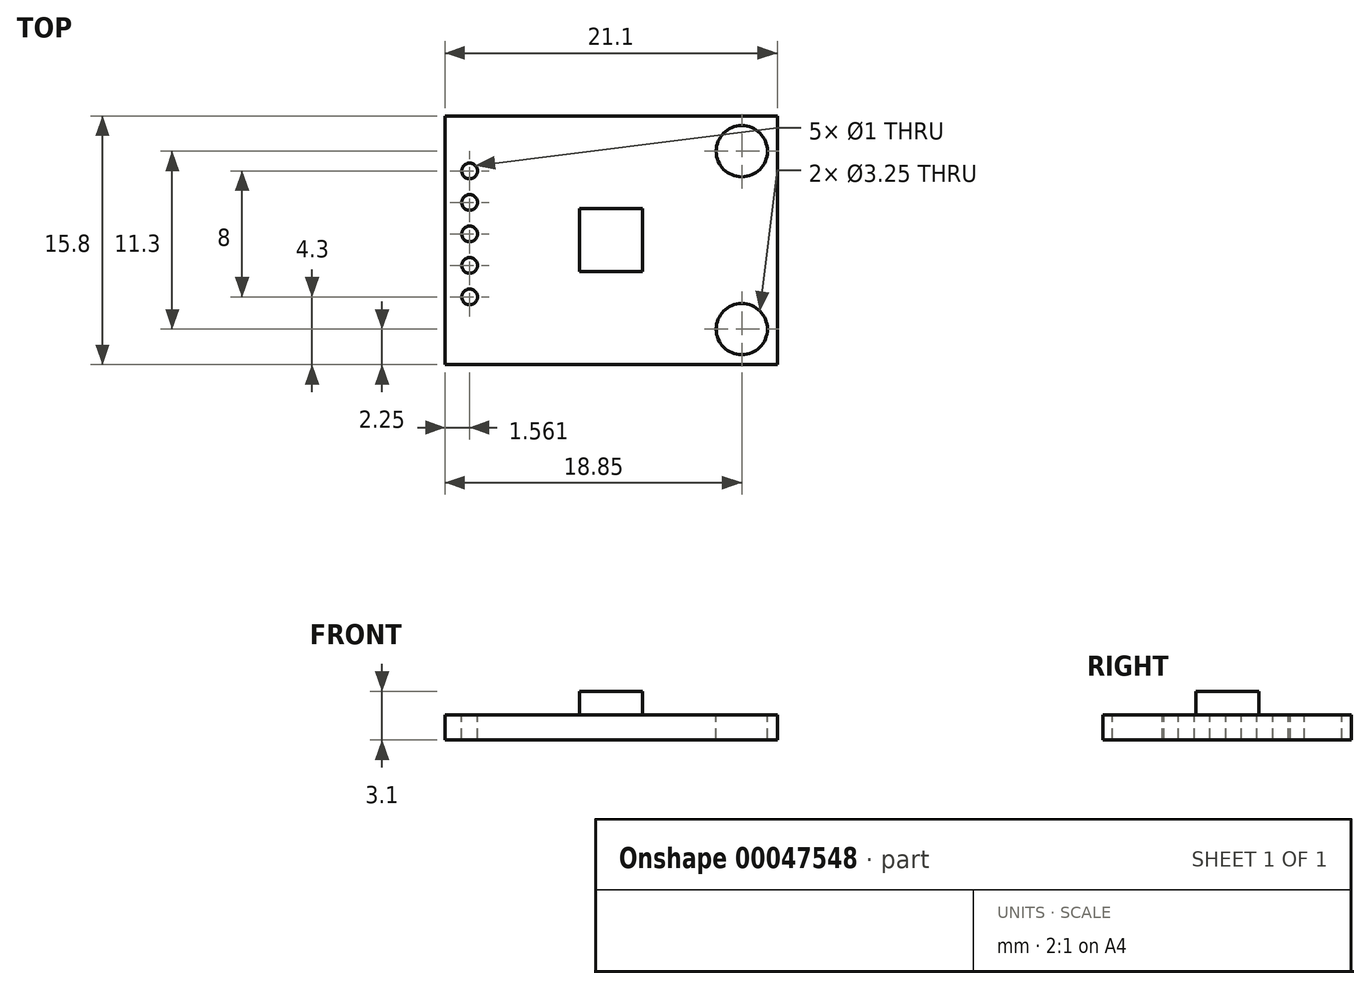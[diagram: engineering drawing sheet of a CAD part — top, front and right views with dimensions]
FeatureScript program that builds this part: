
annotation { "Feature Type Name" : "Feature", "Feature Type Description" : "" }
export const myFeature = defineFeature(function(context is Context, id is Id, definition is map)
    precondition{}
    {
        {
            var Q0;
            Q0=qCreatedBy(makeId("Top.planeOp"),FACE);
            var sketch = newSketch(context, id + "F0", { "sketchPlane" : qUnion([Q0])});
            skLineSegment(sketch, "E0.bottom", {"start": v(-10.55, 7.9) * mm, "end": v(10.55, 7.9) * mm});
            skLineSegment(sketch, "E0.top", {"start": v(-10.55, -7.9) * mm, "end": v(10.55, -7.9) * mm});
            skLineSegment(sketch, "E0.left", {"start": v(-10.55, 7.9) * mm, "end": v(-10.55, -7.9) * mm});
            skLineSegment(sketch, "E0.right", {"start": v(10.55, 7.9) * mm, "end": v(10.55, -7.9) * mm});
            skSolve(sketch);
        }
        {
            var Q0;
            Q0 = qSketchRegion(id + "F0", true);
            extrude(context, id + "F1", {"entities" : qUnion([Q0]), "depth" : 1.6 * mm});
        }
        {
            var Q0;
            Q0=makeQuery(id+"F1.opExtrude","CAP_FACE",FACE,{"disambiguationData":[OSD([sQuery(id+"F0.wireOp",EDGE,"E0.bottom"),sQuery(id+"F0.wireOp",EDGE,"E0.top"),sQuery(id+"F0.wireOp",EDGE,"E0.left"),sQuery(id+"F0.wireOp",EDGE,"E0.right")])],"isStart":false});
            var sketch = newSketch(context, id + "F2", { "sketchPlane" : qUnion([Q0])});
            skCircle(sketch, "E1", {"center": v(8.3, 5.65) * mm, "radius": 1.63 * mm});
            skCircle(sketch, "E2", {"center": v(8.3, -5.65) * mm, "radius": 1.63 * mm});
            skSolve(sketch);
        }
        {
            var Q0;
            Q0 = qSketchRegion(id + "F2", true);
            extrude(context, id + "F3", {"entities" : qUnion([Q0]), "operationType" : NewBodyOperationType.REMOVE, "oppositeDirection" : true, "depth" : 25 * mm});
        }
        {
            var Q0;
            Q0=makeQuery(id+"F1.opExtrude","CAP_FACE",FACE,{"disambiguationData":[OSD([sQuery(id+"F0.wireOp",EDGE,"E0.bottom"),sQuery(id+"F0.wireOp",EDGE,"E0.top"),sQuery(id+"F0.wireOp",EDGE,"E0.left"),sQuery(id+"F0.wireOp",EDGE,"E0.right")])],"isStart":false});
            var sketch = newSketch(context, id + "F4", { "sketchPlane" : qUnion([Q0])});
            skLineSegment(sketch, "E3.bottom", {"start": v(-2, 2) * mm, "end": v(2, 2) * mm});
            skLineSegment(sketch, "E3.top", {"start": v(-2, -2) * mm, "end": v(2, -2) * mm});
            skLineSegment(sketch, "E3.left", {"start": v(-2, 2) * mm, "end": v(-2, -2) * mm});
            skLineSegment(sketch, "E3.right", {"start": v(2, 2) * mm, "end": v(2, -2) * mm});
            skSolve(sketch);
        }
        {
            var Q0;
            Q0 = qSketchRegion(id + "F4", true);
            extrude(context, id + "F5", {"entities" : qUnion([Q0]), "operationType" : NewBodyOperationType.ADD, "depth" : 1.5 * mm});
        }
        {
            var Q0;
            Q0=makeQuery(id+"F1.opExtrude","CAP_FACE",FACE,{"disambiguationData":[OSD([sQuery(id+"F0.wireOp",EDGE,"E0.bottom"),sQuery(id+"F0.wireOp",EDGE,"E0.top"),sQuery(id+"F0.wireOp",EDGE,"E0.left"),sQuery(id+"F0.wireOp",EDGE,"E0.right")])],"isStart":false});
            var sketch = newSketch(context, id + "F6", { "sketchPlane" : qUnion([Q0])});
            skCircle(sketch, "E4", {"center": v(-8.99, 4.4) * mm, "radius": 0.5 * mm});
            skCircle(sketch, "E5", {"center": v(-8.99, 2.4) * mm, "radius": 0.5 * mm});
            skCircle(sketch, "E6", {"center": v(-8.99, 0.4) * mm, "radius": 0.5 * mm});
            skCircle(sketch, "E7", {"center": v(-8.99, -1.6) * mm, "radius": 0.5 * mm});
            skCircle(sketch, "E8", {"center": v(-8.99, -3.6) * mm, "radius": 0.5 * mm});
            skSolve(sketch);
        }
        {
            var Q0;
            Q0 = qSketchRegion(id + "F6", true);
            extrude(context, id + "F7", {"entities" : qUnion([Q0]), "operationType" : NewBodyOperationType.REMOVE, "oppositeDirection" : true, "depth" : 25 * mm});
        }
    });
